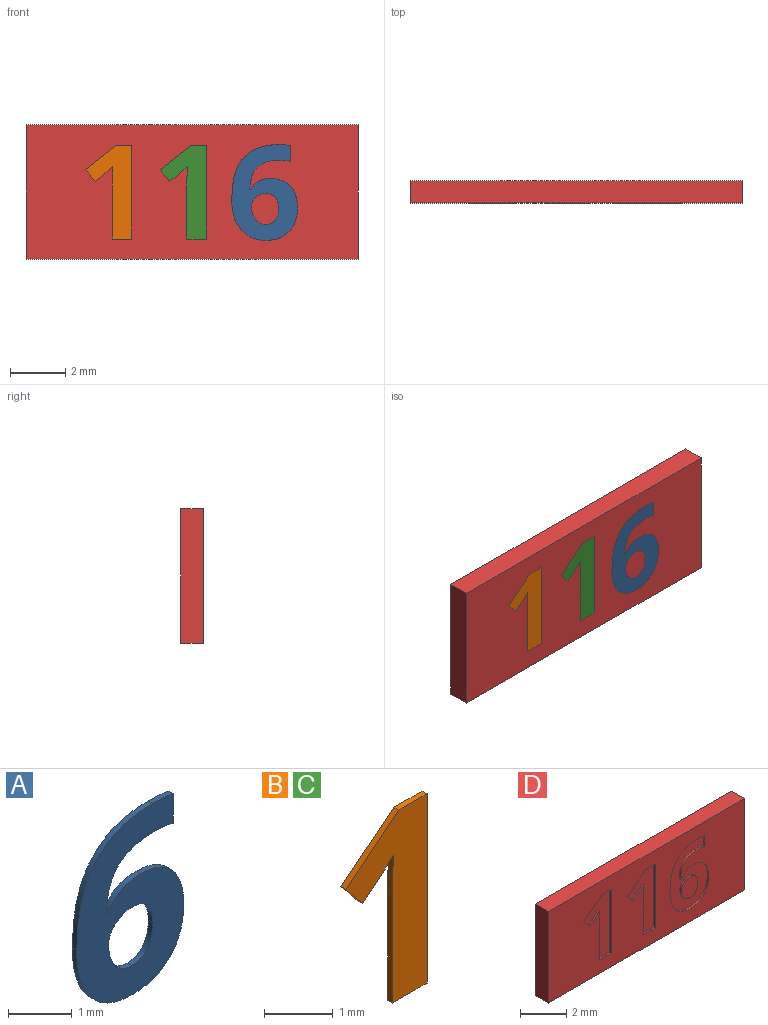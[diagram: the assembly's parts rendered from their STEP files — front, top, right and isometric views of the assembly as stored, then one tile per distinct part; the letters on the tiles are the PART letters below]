
ASSEMBLY  parts=4 mates=3
PART A: 27 faces, bbox 2.4x0.1x3.5 mm
  f0: plane 3.46x2.38mm, normal (0,-1,0), area 4.8mm2, adj f1,f2,f3,f4,f5,f6,f7,f8
  f1: extruded ~0.51x0.43mm, area 0.1mm2, adj f0,f2,f20,f22
  f2: extruded ~0.65x0.17mm, area 0.1mm2, adj f0,f1,f3,f20
  f3: extruded ~0.84x0.32mm, area 0.1mm2, adj f0,f2,f4,f20
  f4: extruded ~0.85x0.3mm, area 0.1mm2, adj f0,f3,f5,f20
  f5: extruded ~0.78x0.26mm, area 0.1mm2, adj f0,f4,f6,f20
  f6: extruded ~0.71x0.28mm, area 0.1mm2, adj f0,f5,f7,f20
  f7: extruded ~0.73x0.39mm, area 0.1mm2, adj f0,f6,f8,f20
  f8: plane 0.1x0.03mm, normal (0,0,1), area 0mm2, adj f0,f7,f9,f20
  f9: extruded ~0.62x0.14mm, area 0.1mm2, adj f0,f8,f10,f20
  f10: extruded ~0.35x0.33mm, area 0mm2, adj f0,f9,f11,f20
  f11: extruded ~0.6x0.11mm, area 0.1mm2, adj f0,f10,f12,f20
  f12: extruded ~0.41x0.1mm, area 0mm2, adj f0,f11,f13,f20
  f13: plane 0.57x0.1mm, normal (1,0,0), area 0.1mm2, adj f0,f12,f14,f20
  f14: extruded ~0.45x0.1mm, area 0mm2, adj f0,f13,f20,f21
  f15: extruded ~0.46x0.14mm, area 0mm2, adj f0,f16,f20,f25
  f16: extruded ~0.33x0.15mm, area 0mm2, adj f0,f15,f17,f20
  f17: extruded ~0.37x0.14mm, area 0mm2, adj f0,f16,f18,f20
  f18: extruded ~0.34x0.14mm, area 0mm2, adj f0,f17,f19,f20
  f19: extruded ~0.39x0.11mm, area 0mm2, adj f0,f18,f20,f24
  f20: plane 3.46x2.38mm, normal (0,1,0), area 4.8mm2, adj f1,f2,f3,f4,f5,f6,f7,f8
  f21: extruded ~1.27x0.49mm, area 0.1mm2, adj f0,f14,f20,f23
  f22: extruded ~0.8x0.15mm, area 0.1mm2, adj f0,f1,f20,f23
  f23: extruded ~1.49x0.42mm, area 0.2mm2, adj f0,f20,f21,f22
  f24: extruded ~0.44x0.12mm, area 0mm2, adj f0,f19,f20,f26
  f25: extruded ~0.37x0.19mm, area 0mm2, adj f0,f15,f20,f26
  f26: extruded ~0.35x0.15mm, area 0mm2, adj f0,f20,f24,f25
PART B: 12 faces, bbox 1.7x0.1x3.4 mm
  f0: plane 3.37x1.67mm, normal (0,-1,0), area 2.9mm2, adj f1,f2,f3,f4,f5,f6,f7,f9
  f1: plane 0.59x0.1mm, normal (0,0,1), area 0.1mm2, adj f0,f2,f8,f10
  f2: plane 1.09x0.86mm, normal (-0.62,0,0.78), area 0.1mm2, adj f0,f1,f3,f8
  f3: plane 0.43x0.34mm, normal (-0.78,0,-0.63), area 0.1mm2, adj f0,f2,f4,f8
  f4: plane 0.39x0.31mm, normal (0.63,0,-0.78), area 0mm2, adj f0,f3,f5,f8
  f5: extruded ~0.25x0.23mm, area 0mm2, adj f0,f4,f6,f8
  f6: plane 0.35x0.1mm, normal (-1,0,0.03), area 0mm2, adj f0,f5,f7,f8
  f7: plane 0.32x0.1mm, normal (-1,0,0.02), area 0mm2, adj f0,f6,f8,f9
  f8: plane 3.37x1.67mm, normal (0,1,0), area 2.9mm2, adj f1,f2,f3,f4,f5,f6,f7,f9
  f9: plane 1.95x0.1mm, normal (-1,0,0), area 0.2mm2, adj f0,f7,f8,f11
  f10: plane 3.37x0.1mm, normal (1,0,0), area 0.3mm2, adj f0,f1,f8,f11
  f11: plane 0.71x0.1mm, normal (0,0,-1), area 0.1mm2, adj f0,f8,f9,f10
PART C: same geometry as B
PART D: 55 faces, bbox 12x0.8x4.9 mm
  f0: plane 12x4.85mm, normal (0,-1,0), area 46.6mm2, adj f1,f2,f3,f4,f6,f7,f8,f9
  f1: plane 12x0.8mm, normal (0,0,-1), area 9.6mm2, adj f0,f2,f4,f5
  f2: plane 4.85x0.8mm, normal (1,0,0), area 3.9mm2, adj f0,f1,f3,f5
  f3: plane 12x0.8mm, normal (0,0,1), area 9.6mm2, adj f0,f2,f4,f5
  f4: plane 4.85x0.8mm, normal (-1,0,0), area 3.9mm2, adj f0,f1,f3,f5
  f5: plane 12x4.85mm, normal (0,1,0), area 58.2mm2, adj f1,f2,f3,f4
  f6: extruded ~0.8x0.15mm, area 0.1mm2, adj f0,f7,f30,f31
  f7: extruded ~0.51x0.43mm, area 0.1mm2, adj f0,f6,f8,f31
  f8: extruded ~0.65x0.17mm, area 0.1mm2, adj f0,f7,f9,f31
  f9: extruded ~0.84x0.32mm, area 0.1mm2, adj f0,f8,f10,f31
  f10: extruded ~0.85x0.3mm, area 0.1mm2, adj f0,f9,f11,f31
  f11: extruded ~0.78x0.26mm, area 0.1mm2, adj f0,f10,f12,f31
  f12: extruded ~0.71x0.28mm, area 0.1mm2, adj f0,f11,f13,f31
  f13: extruded ~0.73x0.39mm, area 0.1mm2, adj f0,f12,f14,f31
  f14: plane 0.1x0.03mm, normal (0,0,-1), area 0mm2, adj f0,f13,f15,f31
  f15: extruded ~0.62x0.14mm, area 0.1mm2, adj f0,f14,f16,f31
  f16: extruded ~0.35x0.33mm, area 0mm2, adj f0,f15,f17,f31
  f17: extruded ~0.6x0.11mm, area 0.1mm2, adj f0,f16,f18,f31
  f18: extruded ~0.41x0.1mm, area 0mm2, adj f0,f17,f19,f31
  f19: plane 0.57x0.1mm, normal (-1,0,0), area 0.1mm2, adj f0,f18,f20,f31
  f20: extruded ~0.45x0.1mm, area 0mm2, adj f0,f19,f21,f31
  f21: extruded ~1.27x0.49mm, area 0.1mm2, adj f0,f20,f30,f31
  f22: extruded ~0.37x0.19mm, area 0mm2, adj f23,f29,f31,f32
  f23: extruded ~0.46x0.14mm, area 0mm2, adj f22,f24,f31,f32
  f24: extruded ~0.33x0.15mm, area 0mm2, adj f23,f25,f31,f32
  f25: extruded ~0.37x0.14mm, area 0mm2, adj f24,f26,f31,f32
  f26: extruded ~0.34x0.14mm, area 0mm2, adj f25,f27,f31,f32
  f27: extruded ~0.39x0.11mm, area 0mm2, adj f26,f28,f31,f32
  f28: extruded ~0.44x0.12mm, area 0mm2, adj f27,f29,f31,f32
  f29: extruded ~0.35x0.15mm, area 0mm2, adj f22,f28,f31,f32
  f30: extruded ~1.49x0.42mm, area 0.2mm2, adj f0,f6,f21,f31
  f31: plane 3.46x2.38mm, normal (0,-1,0), area 4.8mm2, adj f6,f7,f8,f9,f10,f11,f12,f13
  f32: plane 1.12x0.98mm, normal (0,-1,0), area 0.9mm2, adj f22,f23,f24,f25,f26,f27,f28,f29
  f33: plane 3.37x0.1mm, normal (-1,0,0), area 0.3mm2, adj f0,f34,f42,f43
  f34: plane 0.59x0.1mm, normal (0,0,-1), area 0.1mm2, adj f0,f33,f35,f43
  f35: plane 1.09x0.86mm, normal (0.62,0,-0.78), area 0.1mm2, adj f0,f34,f36,f43
  f36: plane 0.43x0.34mm, normal (0.78,0,0.63), area 0.1mm2, adj f0,f35,f37,f43
  f37: plane 0.39x0.31mm, normal (-0.63,0,0.78), area 0mm2, adj f0,f36,f38,f43
  f38: extruded ~0.25x0.23mm, area 0mm2, adj f0,f37,f39,f43
  f39: plane 0.35x0.1mm, normal (1,0,-0.03), area 0mm2, adj f0,f38,f40,f43
  f40: plane 0.32x0.1mm, normal (1,0,-0.02), area 0mm2, adj f0,f39,f41,f43
  f41: plane 1.95x0.1mm, normal (1,0,0), area 0.2mm2, adj f0,f40,f42,f43
  f42: plane 0.71x0.1mm, normal (0,0,1), area 0.1mm2, adj f0,f33,f41,f43
  f43: plane 3.37x1.67mm, normal (0,-1,0), area 2.9mm2, adj f33,f34,f35,f36,f37,f38,f39,f40
  f44: plane 3.37x0.1mm, normal (-1,0,0), area 0.3mm2, adj f0,f45,f53,f54
  f45: plane 0.59x0.1mm, normal (0,0,-1), area 0.1mm2, adj f0,f44,f46,f54
  f46: plane 1.09x0.86mm, normal (0.62,0,-0.78), area 0.1mm2, adj f0,f45,f47,f54
  f47: plane 0.43x0.34mm, normal (0.78,0,0.63), area 0.1mm2, adj f0,f46,f48,f54
  f48: plane 0.39x0.31mm, normal (-0.63,0,0.78), area 0mm2, adj f0,f47,f49,f54
  f49: extruded ~0.25x0.23mm, area 0mm2, adj f0,f48,f50,f54
  f50: plane 0.35x0.1mm, normal (1,0,-0.03), area 0mm2, adj f0,f49,f51,f54
  f51: plane 0.32x0.1mm, normal (1,0,-0.02), area 0mm2, adj f0,f50,f52,f54
  f52: plane 1.95x0.1mm, normal (1,0,0), area 0.2mm2, adj f0,f51,f53,f54
  f53: plane 0.71x0.1mm, normal (0,0,1), area 0.1mm2, adj f0,f44,f52,f54
  f54: plane 3.37x1.67mm, normal (0,-1,0), area 2.9mm2, adj f44,f45,f46,f47,f48,f49,f50,f51
PLACE A t=(1.13,0.4,0)mm
PLACE B t=(-4.56,0.4,0)mm
PLACE C t=(-1.86,0.4,0)mm
PLACE D t=(0,0.4,0)mm
MATE fastened B.f0 <-> D.f0  axis (0,-1,0) through (-2.88,-0.4,-1.7)mm
MATE fastened C.f0 <-> D.f0  axis (0,-1,0) through (-0.19,-0.4,-1.7)mm
MATE fastened A.f0 <-> D.f0  axis (0,-1,0) through (3.58,-0.4,1.1)mm
